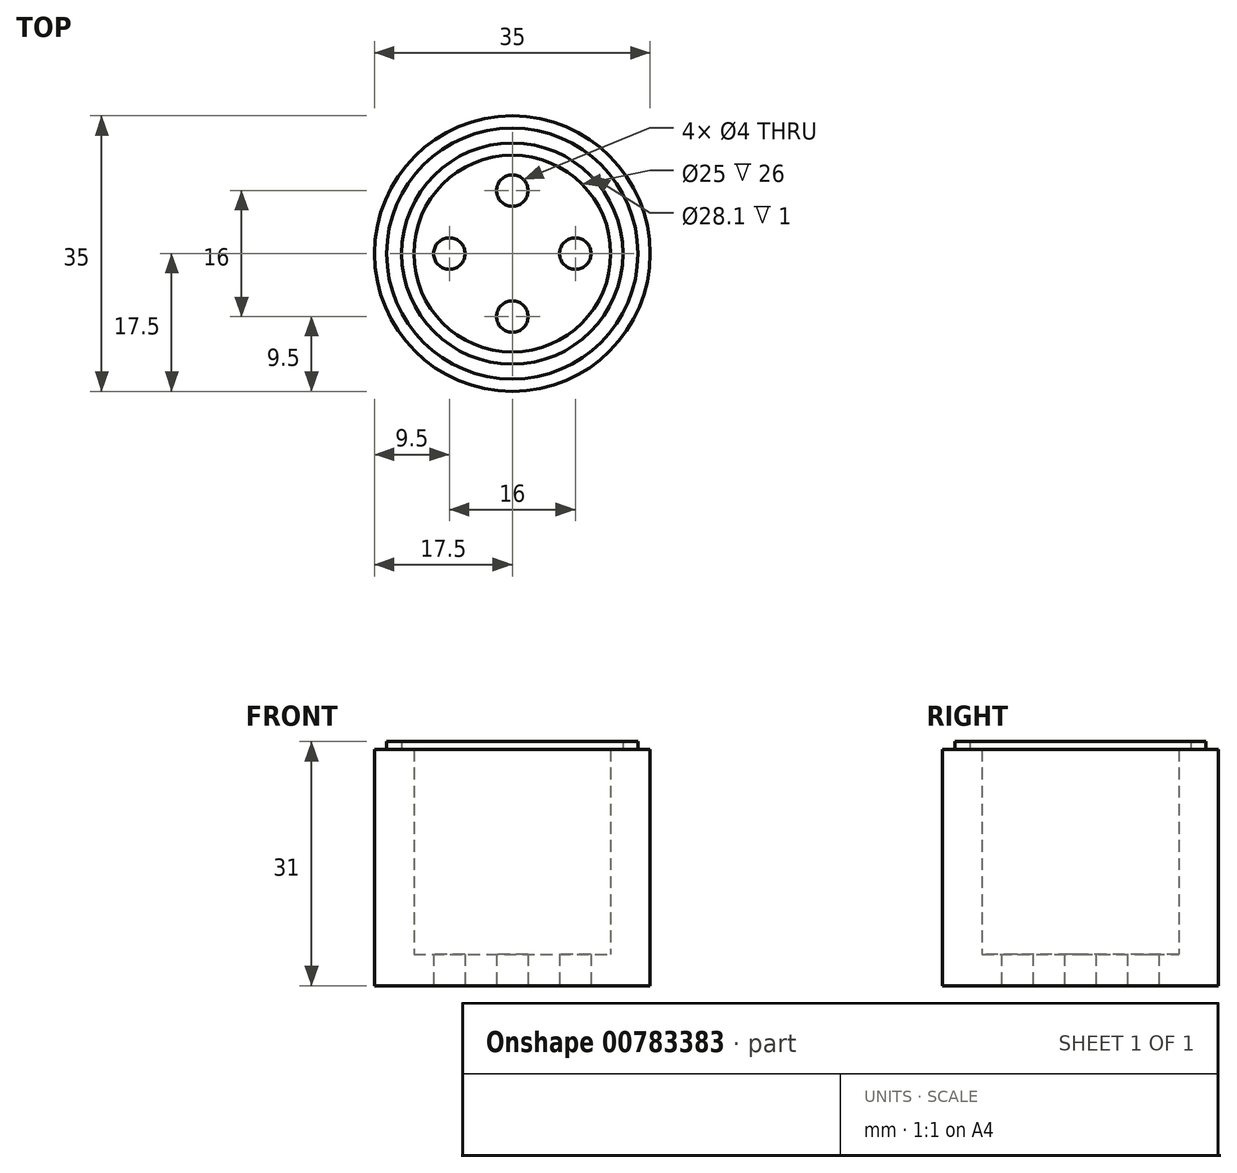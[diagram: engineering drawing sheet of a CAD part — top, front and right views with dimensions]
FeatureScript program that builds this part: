
annotation { "Feature Type Name" : "Feature", "Feature Type Description" : "" }
export const myFeature = defineFeature(function(context is Context, id is Id, definition is map)
    precondition{}
    {
        {
            var Q0;
            Q0=qCreatedBy(makeId("Right.planeOp"),FACE);
            var sketch = newSketch(context, id + "F0", { "sketchPlane" : qUnion([Q0])});
            skLineSegment(sketch, "E0", {"start": v(0, 0) * mm, "end": v(-17.5, 0) * mm});
            skLineSegment(sketch, "E1", {"start": v(-17.5, 0) * mm, "end": v(-17.5, 30) * mm});
            skLineSegment(sketch, "E2", {"start": v(-17.5, 30) * mm, "end": v(-12.5, 30) * mm});
            skLineSegment(sketch, "E3", {"start": v(-12.5, 30) * mm, "end": v(-12.5, 4) * mm});
            skLineSegment(sketch, "E4", {"start": v(-12.5, 4) * mm, "end": v(0, 4) * mm});
            skLineSegment(sketch, "E5", {"start": v(0, 4) * mm, "end": v(0, 0) * mm});
            skLineSegment(sketch, "E6", {"start": v(-14.05, 30) * mm, "end": v(-14.05, 31) * mm});
            skLineSegment(sketch, "E7", {"start": v(-14.05, 31) * mm, "end": v(-15.95, 31) * mm});
            skLineSegment(sketch, "E8", {"start": v(-15.95, 31) * mm, "end": v(-15.95, 30) * mm});
            skLineSegment(sketch, "E9", {"start": v(0, 0) * mm, "end": v(0, 58.1) * mm});
            skPoint(sketch, "E9.endSnap0", {"position": v(0, 2) * mm});
            skSolve(sketch);
        }
        {
            var Q0;
            {var subQ3=sQuery(id+"F0.wireOp",EDGE,"E6");Q0=qUnion([makeQuery(id+"F0.imprint","IMPRINT",FACE,{"disambiguationData":[TD([[makeQuery(id+"F0.imprint","IMPRINT",EDGE,{"derivedFrom":sQuery(id+"F0.wireOp",EDGE,"E0")}),-1.0]])]}),makeQuery(id+"F0.imprint","IMPRINT",FACE,{"disambiguationData":[TD([[makeQuery(id+"F0.imprint","IMPRINT",EDGE,{"derivedFrom":subQ3}),1.0]])]})]);}
            var Q1;
            Q1=sQuery(id+"F0.wireOp",EDGE,"E9");
            revolve(context, id + "F1", {"surfaceOperationType" : NewSurfaceOperationType.NEW, "entities" : qUnion([Q0]), "axis" : qUnion([Q1]), "revolveType" : RevolveType.FULL});
        }
        {
            var Q0;
            Q0=qCreatedBy(makeId("Top.planeOp"),FACE);
            var sketch = newSketch(context, id + "F2", { "sketchPlane" : qUnion([Q0])});
            skLineSegment(sketch, "E10", {"start": v(0, 0) * mm, "end": v(0, -8) * mm});
            skLineSegment(sketch, "E11", {"start": v(0, 0) * mm, "end": v(8, 0) * mm});
            skLineSegment(sketch, "E12", {"start": v(0, 0) * mm, "end": v(0, 8) * mm});
            skLineSegment(sketch, "E13", {"start": v(0, 0) * mm, "end": v(-8, 0) * mm});
            skSolve(sketch);
        }
        {
            var Q0;
            Q0=sQuery(id+"F2.wireOp",VERTEX,"E11.end");
            var Q1;
            Q1=sQuery(id+"F2.wireOp",VERTEX,"E12.end");
            var Q2;
            Q2=sQuery(id+"F2.wireOp",VERTEX,"E10.end");
            var Q3;
            Q3=sQuery(id+"F2.wireOp",VERTEX,"E13.end");
            var Q4;
            Q4=makeQuery(id+"F1.opRevolve","SWEPT_BODY",BODY,{"disambiguationData":[OSD([sQuery(id+"F0.wireOp",EDGE,"E0"),sQuery(id+"F0.wireOp",EDGE,"E1"),sQuery(id+"F0.wireOp",EDGE,"E2"),sQuery(id+"F0.wireOp",EDGE,"E3"),sQuery(id+"F0.wireOp",EDGE,"E4"),sQuery(id+"F0.wireOp",EDGE,"E5"),sQuery(id+"F0.wireOp",EDGE,"E6"),sQuery(id+"F0.wireOp",EDGE,"E7"),sQuery(id+"F0.wireOp",EDGE,"E8")])]});
            hole(context, id + "F3", {"style" : HoleStyle.SIMPLE, "endStyle" : HoleEndStyle.THROUGH, "oppositeDirection" : true, "holeDiameter" : 4 * mm, "majorDiameter" : 5 * mm, "isTappedThrough" : true, "tappedDepth" : 12 * mm, "tapClearance" : 3, "locations" : qUnion([Q0, Q1, Q2, Q3]), "scope" : qUnion([Q4])});
        }
    });
